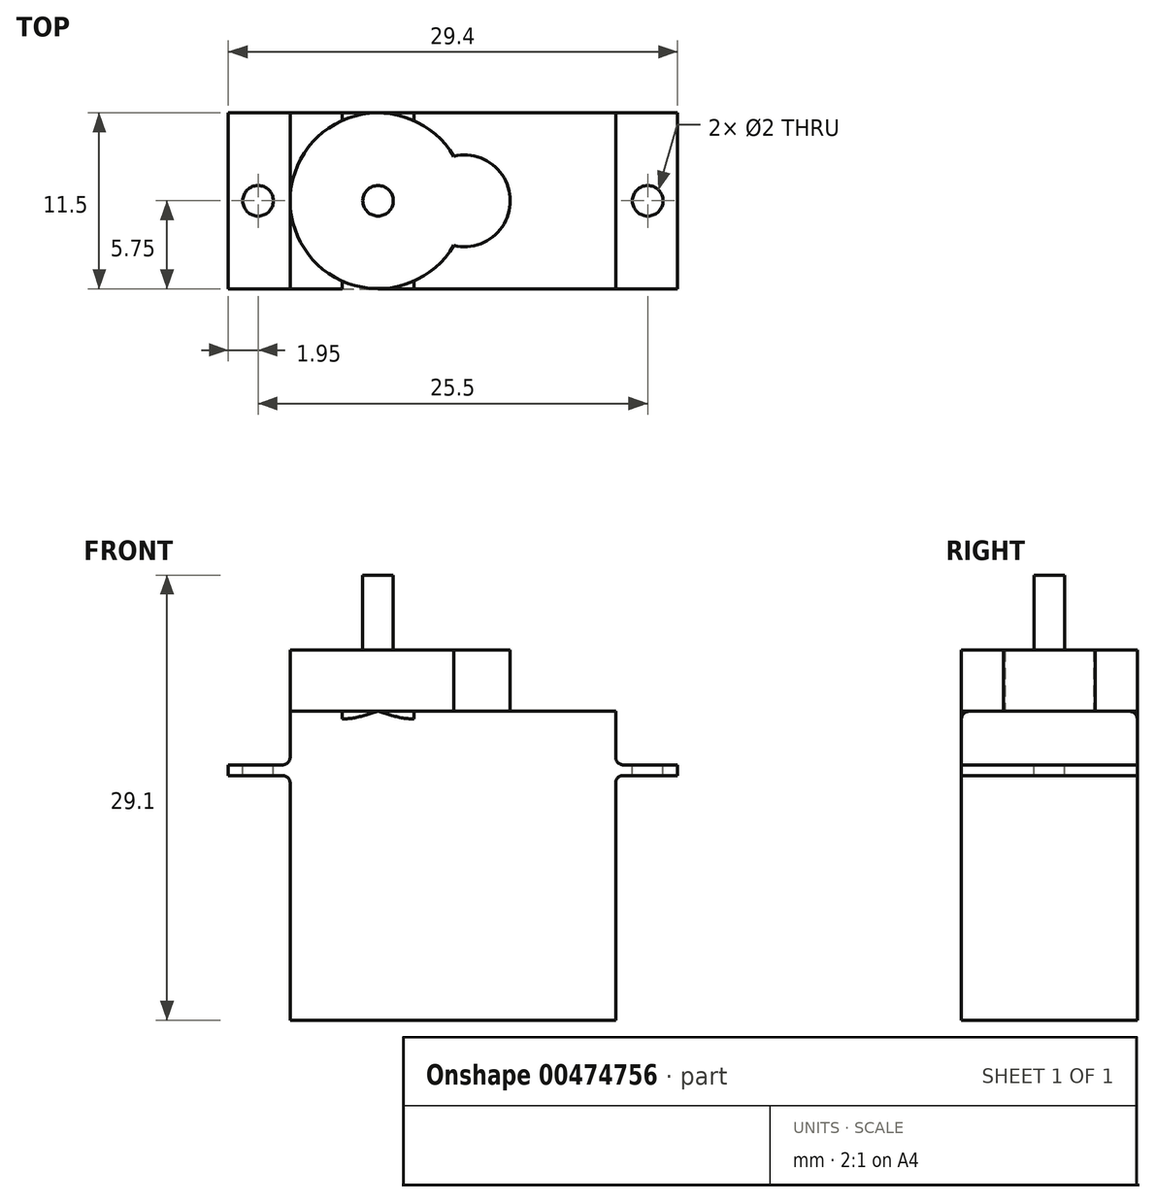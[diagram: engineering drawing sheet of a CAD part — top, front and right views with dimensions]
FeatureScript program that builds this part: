
annotation { "Feature Type Name" : "Feature", "Feature Type Description" : "" }
export const myFeature = defineFeature(function(context is Context, id is Id, definition is map)
    precondition{}
    {
        {
            var Q0;
            Q0=qCreatedBy(makeId("Front.planeOp"),FACE);
            var sketch = newSketch(context, id + "F0", { "sketchPlane" : qUnion([Q0])});
            skLineSegment(sketch, "E0.bottom", {"start": v(0, 0) * mm, "end": v(21.3, 0) * mm});
            skLineSegment(sketch, "E0.top", {"start": v(0, 20.2) * mm, "end": v(21.3, 20.2) * mm});
            skLineSegment(sketch, "E0.left", {"start": v(0, 0) * mm, "end": v(0, 16) * mm});
            skLineSegment(sketch, "E0.right", {"start": v(21.3, 0) * mm, "end": v(21.3, 16) * mm});
            skLineSegment(sketch, "E1.bottom", {"start": v(-4.05, 16.7) * mm, "end": v(0, 16.7) * mm});
            skLineSegment(sketch, "E1.top", {"start": v(-4.05, 16) * mm, "end": v(0, 16) * mm});
            skLineSegment(sketch, "E1.left", {"start": v(-4.05, 16.7) * mm, "end": v(-4.05, 16) * mm});
            skLineSegment(sketch, "E1.right", {"start": v(25.35, 16.7) * mm, "end": v(25.35, 16) * mm});
            skLineSegment(sketch, "E2.trimOffspring", {"start": v(0, 16.7) * mm, "end": v(0, 20.2) * mm});
            skLineSegment(sketch, "E3.trimOffspring", {"start": v(21.3, 16.7) * mm, "end": v(25.35, 16.7) * mm});
            skLineSegment(sketch, "E4.trimOffspring", {"start": v(21.3, 16) * mm, "end": v(25.35, 16) * mm});
            skLineSegment(sketch, "E5.trimOffspring", {"start": v(21.3, 16.7) * mm, "end": v(21.3, 20.2) * mm});
            skSolve(sketch);
        }
        {
            var Q0;
            Q0 = qSketchRegion(id + "F0", true);
            extrude(context, id + "F1", {"entities" : qUnion([Q0]), "depth" : 11.5 * mm, "offsetDistance" : 25 * mm});
        }
        {
            var Q0;
            Q0=makeQuery(id+"F1.opExtrude","SWEPT_FACE",FACE,{"disambiguationData":[OSD([sQuery(id+"F0.wireOp",EDGE,"E0.top")])]});
            var sketch = newSketch(context, id + "F2", { "sketchPlane" : qUnion([Q0])});
            skArc(sketch, "E6", {"start": v(10.7, -2.83) * mm, "mid": v(0, -5.75) * mm, "end": v(10.7, -8.67) * mm});
            skLineSegment(sketch, "E7", {"start": v(0, -5.75) * mm, "end": v(21.3, -5.75) * mm, "construction": true});
            skArc(sketch, "E8", {"start": v(10.7, -8.67) * mm, "mid": v(14.4, -5.75) * mm, "end": v(10.7, -2.83) * mm});
            skSolve(sketch);
        }
        {
            var Q0;
            Q0 = qSketchRegion(id + "F2", true);
            extrude(context, id + "F3", {"entities" : qUnion([Q0]), "operationType" : NewBodyOperationType.ADD, "depth" : 4 * mm, "offsetDistance" : 25 * mm});
        }
        {
            var Q0;
            Q0=makeQuery(id+"F1.opExtrude","SWEPT_FACE",FACE,{"disambiguationData":[OSD([sQuery(id+"F0.wireOp",EDGE,"E1.bottom")])]});
            var sketch = newSketch(context, id + "F4", { "sketchPlane" : qUnion([Q0])});
            skLineSegment(sketch, "E9", {"start": v(0, -5.75) * mm, "end": v(-4.05, -5.75) * mm, "construction": true});
            skCircle(sketch, "E10", {"center": v(-2.1, -5.75) * mm, "radius": 1 * mm});
            skSolve(sketch);
        }
        {
            var Q0;
            Q0 = qSketchRegion(id + "F4", true);
            extrude(context, id + "F5", {"entities" : qUnion([Q0]), "operationType" : NewBodyOperationType.REMOVE, "endBound" : BoundingType.UP_TO_NEXT, "oppositeDirection" : true, "depth" : 25 * mm, "offsetDistance" : 25 * mm});
        }
        {
            var Q0;
            Q0=makeQuery(id+"F1.opExtrude","SWEPT_FACE",FACE,{"disambiguationData":[OSD([sQuery(id+"F0.wireOp",EDGE,"E3.trimOffspring")])]});
            var sketch = newSketch(context, id + "F6", { "sketchPlane" : qUnion([Q0])});
            skLineSegment(sketch, "E11", {"start": v(21.3, -5.75) * mm, "end": v(25.35, -5.75) * mm, "construction": true});
            skCircle(sketch, "E12", {"center": v(23.4, -5.75) * mm, "radius": 1 * mm});
            skSolve(sketch);
        }
        {
            var Q0;
            Q0 = qSketchRegion(id + "F6", true);
            extrude(context, id + "F7", {"entities" : qUnion([Q0]), "operationType" : NewBodyOperationType.REMOVE, "endBound" : BoundingType.UP_TO_NEXT, "oppositeDirection" : true, "depth" : 25 * mm, "offsetDistance" : 25 * mm});
        }
        {
            var Q0;
            Q0=makeQuery(id+"F3.opExtrude","CAP_FACE",FACE,{"disambiguationData":[OSD([sQuery(id+"F2.wireOp",EDGE,"E6"),sQuery(id+"F2.wireOp",EDGE,"E8"),sQuery(id+"F2.wireOp",EDGE,"6vi0zH1E-XS2O-oO4M-l53y-rl44IrEdtpfP"),sQuery(id+"F2.wireOp",EDGE,"rb24kUxo-ldOG-6ew3-ucOs-fjg7dMNHaOME")])],"isStart":false});
            var sketch = newSketch(context, id + "F8", { "sketchPlane" : qUnion([Q0])});
            skCircle(sketch, "E13", {"center": v(5.75, -5.75) * mm, "radius": 1 * mm});
            skSolve(sketch);
        }
        {
            var Q0;
            Q0 = qSketchRegion(id + "F8", true);
            extrude(context, id + "F9", {"entities" : qUnion([Q0]), "operationType" : NewBodyOperationType.ADD, "depth" : 4.9 * mm, "offsetDistance" : 25 * mm});
        }
        {
            var Q0;
            Q0=makeQuery(id+"F1.opExtrude","SWEPT_EDGE",EDGE,{"disambiguationData":[OSD([sQuery(id+"F0.wireOp",EDGE,"E1.bottom"),sQuery(id+"F0.wireOp",EDGE,"E2.trimOffspring")])]});
            var Q1;
            Q1=makeQuery(id+"F1.opExtrude","SWEPT_EDGE",EDGE,{"disambiguationData":[OSD([sQuery(id+"F0.wireOp",EDGE,"E0.left"),sQuery(id+"F0.wireOp",EDGE,"E1.top")])]});
            var Q2;
            Q2=makeQuery(id+"F1.opExtrude","SWEPT_EDGE",EDGE,{"disambiguationData":[OSD([sQuery(id+"F0.wireOp",EDGE,"E3.trimOffspring"),sQuery(id+"F0.wireOp",EDGE,"E5.trimOffspring")])]});
            var Q3;
            Q3=makeQuery(id+"F1.opExtrude","SWEPT_EDGE",EDGE,{"disambiguationData":[OSD([sQuery(id+"F0.wireOp",EDGE,"E0.right"),sQuery(id+"F0.wireOp",EDGE,"E4.trimOffspring")])]});
            var Q4;
            Q4=makeQuery(id+"F1.opExtrude","CAP_EDGE",EDGE,{"disambiguationData":[OSD([sQuery(id+"F0.wireOp",EDGE,"E0.top")])],"isStart":true});
            var Q5;
            Q5=makeQuery(id+"F1.opExtrude","CAP_EDGE",EDGE,{"disambiguationData":[OSD([sQuery(id+"F0.wireOp",EDGE,"E0.top")])],"isStart":false});
            fillet(context, id + "F10", {"entities" : qUnion([Q0, Q1, Q2, Q3, Q4, Q5]), "radius" : 0.5 * mm, "tangentPropagation" : true, "allowEdgeOverflow" : false});
        }
    });
